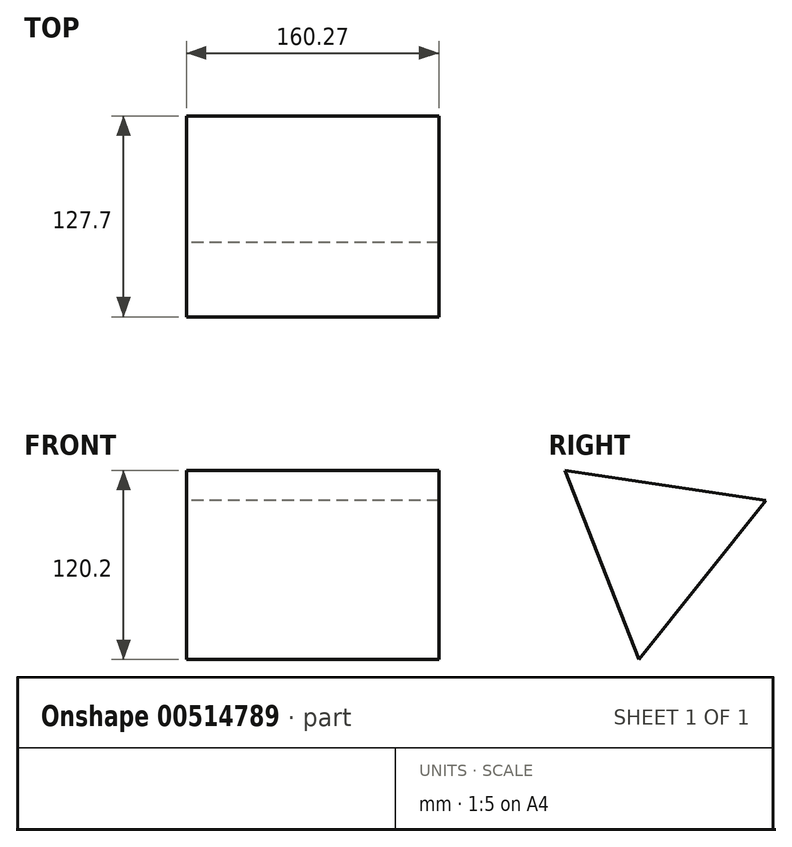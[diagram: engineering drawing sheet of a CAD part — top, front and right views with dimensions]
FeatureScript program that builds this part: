
annotation { "Feature Type Name" : "Feature", "Feature Type Description" : "" }
export const myFeature = defineFeature(function(context is Context, id is Id, definition is map)
    precondition{}
    {
        {
            var Q0;
            Q0=qCreatedBy(makeId("Right.planeOp"),FACE);
            var sketch = newSketch(context, id + "F0", { "sketchPlane" : qUnion([Q0])});
            skCircle(sketch, "E0.cCircle", {"center": v(-34.31, -59.26) * mm, "radius": 37.28 * mm, "construction": true});
            skLineSegment(sketch, "E0.0", {"start": v(-92.61, -12.79) * mm, "end": v(35.09, -32) * mm});
            skLineSegment(sketch, "E0.1", {"start": v(35.09, -32) * mm, "end": v(-45.4, -133) * mm});
            skLineSegment(sketch, "E0.2", {"start": v(-45.4, -133) * mm, "end": v(-92.61, -12.79) * mm});
            skPoint(sketch, "E0.0.midPoint", {"position": v(-28.76, -22.4) * mm});
            skSolve(sketch);
        }
        {
            var Q0;
            Q0 = qSketchRegion(id + "F0", true);
            extrude(context, id + "F1", {"entities" : qUnion([Q0]), "depth" : 160.27 * mm, "offsetDistance" : 25.4 * mm});
        }
    });
